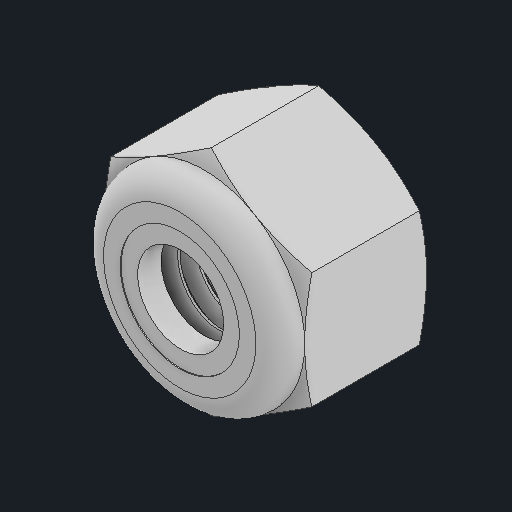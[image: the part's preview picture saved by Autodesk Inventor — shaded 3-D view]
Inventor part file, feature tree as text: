
AUTODESK INVENTOR PART (.ipt)
format: ipt  version: 2024.1 (Build 281209000, 209)  size: 367,104 bytes
history: native  units: in
note: dims shown in document units (in); Inventor stores cm internally (conversion verified against a paired STEP export)
features: revolve x1, other x1
ambient origin geometry x8: Origin, YZ Plane, XZ Plane, XY Plane, X Axis, Y Axis, Z Axis, Center Point
bodies: Solid1 (feature_tree), Solid2 (feature_tree)
feature tree (2):
  revolve  "Revolve1"  [1 undecoded]
  other  "Cut-Extrude2"
note: 1 required parameter value undecoded (feature->parameter linkage not recoverable at this tier; creation-order binding heuristic only, values carry confidence <= 0.55)
